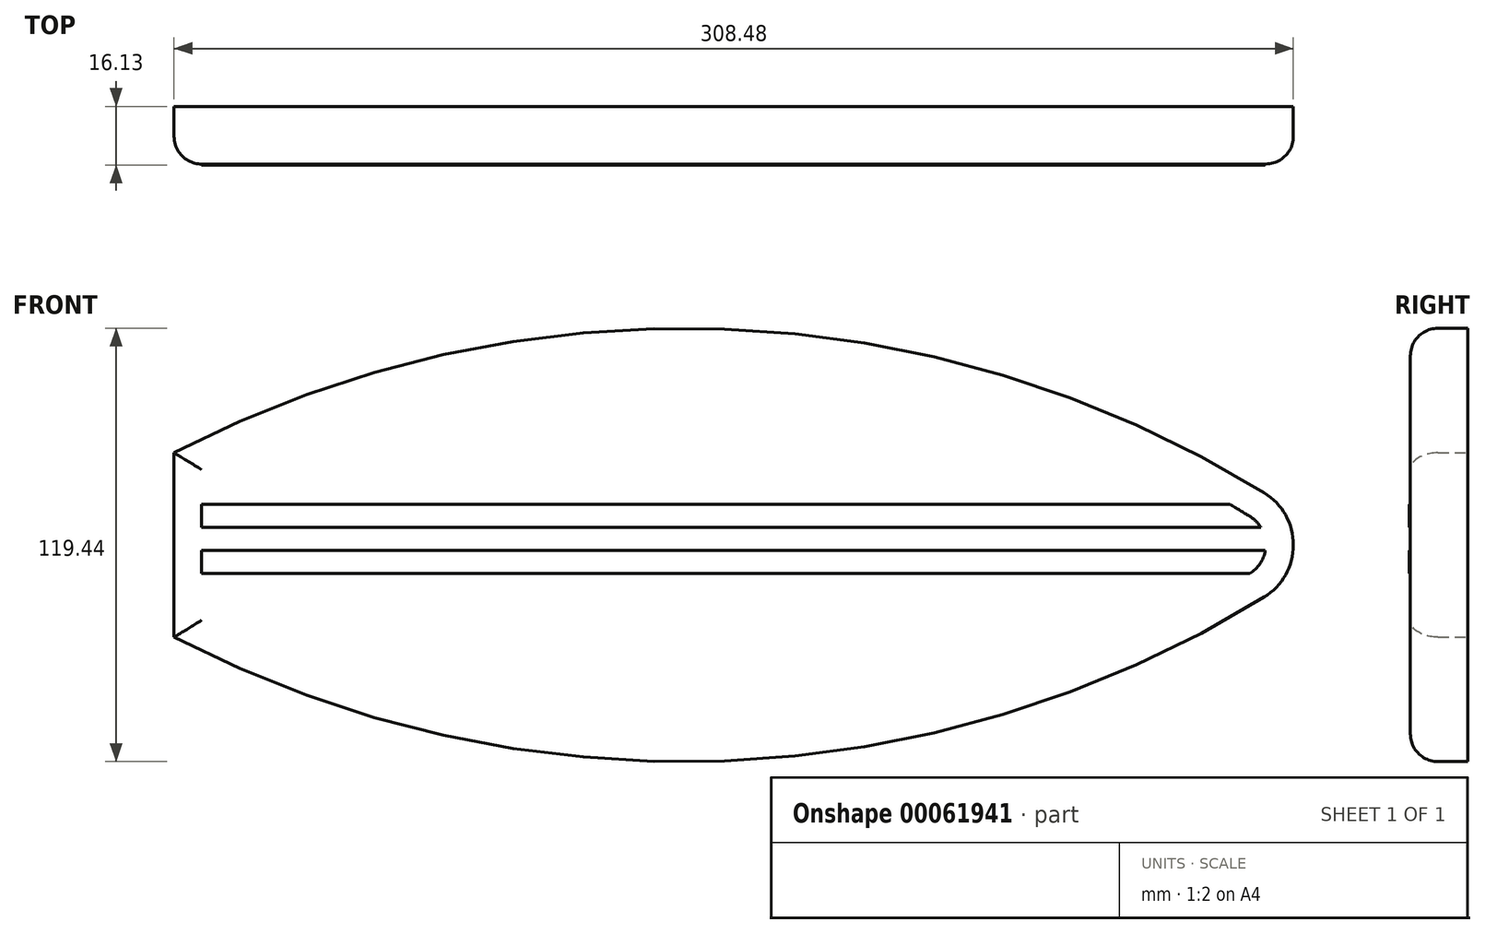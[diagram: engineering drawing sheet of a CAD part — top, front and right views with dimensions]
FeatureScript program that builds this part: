
annotation { "Feature Type Name" : "Feature", "Feature Type Description" : "" }
export const myFeature = defineFeature(function(context is Context, id is Id, definition is map)
    precondition{}
    {
        {
            var Q0;
            Q0=qCreatedBy(makeId("Front.planeOp"),FACE);
            var sketch = newSketch(context, id + "F0", { "sketchPlane" : qUnion([Q0])});
            skArc(sketch, "E0", {"start": v(-292.9, -6.52) * mm, "mid": v(-141.22, -40.63) * mm, "end": v(7.56, 4.51) * mm});
            skPoint(sketch, "E1.visualSharp", {"position": v(-304.8, 0) * mm});
            skLineSegment(sketch, "E1.filletArc", {"start": v(-292.9, -6.52) * mm, "end": v(-292.9, -6.52) * mm});
            skPoint(sketch, "E2.visualSharp", {"position": v(0, 0) * mm});
            skLineSegment(sketch, "E2.filletArc", {"start": v(7.56, 4.51) * mm, "end": v(7.56, 4.51) * mm});
            skLineSegment(sketch, "E3", {"start": v(-292.9, -6.52) * mm, "end": v(-292.9, 44.28) * mm});
            skLineSegment(sketch, "E4", {"start": v(-292.9, 18.88) * mm, "end": v(59.24, 18.88) * mm, "construction": true});
            skArc(sketch, "E5.MirrorCS", {"start": v(-292.9, 44.28) * mm, "mid": v(-141.22, 78.4) * mm, "end": v(7.56, 33.25) * mm});
            skArc(sketch, "E6", {"start": v(7.56, 4.51) * mm, "mid": v(15.58, 18.88) * mm, "end": v(7.56, 33.25) * mm});
            skSolve(sketch);
        }
        {
            var Q0;
            Q0=makeQuery(id+"F0.imprint","IMPRINT",FACE,{"disambiguationData":[TD([[makeQuery(id+"F0.imprint","IMPRINT",EDGE,{"derivedFrom":sQuery(id+"F0.wireOp",EDGE,"E0")}),1.0]])]});
            extrude(context, id + "F1", {"entities" : qUnion([Q0]), "depth" : 15.88 * mm});
        }
        {
            var Q0;
            Q0=makeQuery(id+"F1.opExtrude","CAP_FACE",FACE,{"disambiguationData":[OSD([sQuery(id+"F0.wireOp",EDGE,"E0"),sQuery(id+"F0.wireOp",EDGE,"E3"),sQuery(id+"F0.wireOp",EDGE,"E5.MirrorCS"),sQuery(id+"F0.wireOp",EDGE,"E6")])],"isStart":false});
            fillet(context, id + "F2", {"entities" : qUnion([Q0]), "radius" : 7.62 * mm, "tangentPropagation" : true, "allowEdgeOverflow" : false});
        }
        {
            var Q0;
            Q0=makeQuery(id+"F1.opExtrude","CAP_FACE",FACE,{"disambiguationData":[OSD([sQuery(id+"F0.wireOp",EDGE,"E0"),sQuery(id+"F0.wireOp",EDGE,"E3"),sQuery(id+"F0.wireOp",EDGE,"E5.MirrorCS"),sQuery(id+"F0.wireOp",EDGE,"E6")])],"isStart":false});
            var sketch = newSketch(context, id + "F3", { "sketchPlane" : qUnion([Q0])});
            skLineSegment(sketch, "E7.rect.bottom", {"start": v(7.96, 17.35) * mm, "end": v(-285.28, 17.35) * mm, "construction": true});
            skLineSegment(sketch, "E7.rect.top", {"start": v(7.96, 23.7) * mm, "end": v(-285.28, 23.7) * mm, "construction": true});
            skLineSegment(sketch, "E7.rect.left", {"start": v(7.96, 17.35) * mm, "end": v(7.96, 23.7) * mm, "construction": true});
            skPoint(sketch, "E7.rect.middle", {"position": v(-285.28, 18.88) * mm});
            skPoint(sketch, "E7.rect.cornerSnap0", {"position": v(7.96, 18.88) * mm});
            skLineSegment(sketch, "E8.0", {"start": v(-285.28, 23.7) * mm, "end": v(-285.28, 17.35) * mm, "construction": true});
            skPoint(sketch, "E9.orphan", {"position": v(-285.28, 39.61) * mm});
            skPoint(sketch, "E10.orphan", {"position": v(-285.28, -1.85) * mm});
            skLineSegment(sketch, "E11.bottom", {"start": v(-285.28, 23.7) * mm, "end": v(7.96, 23.7) * mm});
            skLineSegment(sketch, "E11.top", {"start": v(-285.28, 30.05) * mm, "end": v(7.96, 30.05) * mm});
            skLineSegment(sketch, "E11.left", {"start": v(-285.28, 23.7) * mm, "end": v(-285.28, 30.05) * mm});
            skLineSegment(sketch, "E11.right", {"start": v(7.96, 23.7) * mm, "end": v(7.96, 30.05) * mm});
            skLineSegment(sketch, "E12.bottom", {"start": v(7.96, 17.35) * mm, "end": v(-285.28, 17.35) * mm});
            skLineSegment(sketch, "E12.top", {"start": v(7.96, 11) * mm, "end": v(-285.28, 11) * mm});
            skLineSegment(sketch, "E12.left", {"start": v(7.96, 17.35) * mm, "end": v(7.96, 11) * mm});
            skLineSegment(sketch, "E12.right", {"start": v(-285.28, 17.35) * mm, "end": v(-285.28, 11) * mm});
            skSolve(sketch);
        }
        {
            var Q0;
            {var subQ9=sQuery(id+"F3.wireOp",EDGE,"E11.left");Q0=makeQuery(id+"F3.imprint","IMPRINT",FACE,{"disambiguationData":[TD([[makeQuery(id+"F3.imprint","IMPRINT",EDGE,{"derivedFrom":subQ9}),1.0]])]});}
            var Q1;
            {var subQ0=sQuery(id+"F3.wireOp",EDGE,"E12.right");Q1=makeQuery(id+"F3.imprint","IMPRINT",FACE,{"disambiguationData":[TD([[makeQuery(id+"F3.imprint","IMPRINT",EDGE,{"derivedFrom":subQ0}),1.0]])]});}
            extrude(context, id + "F4", {"entities" : qUnion([Q0, Q1]), "depth" : 0.25 * mm});
        }
    });
